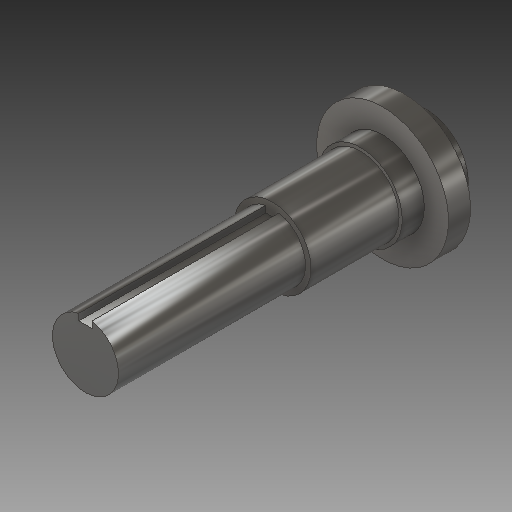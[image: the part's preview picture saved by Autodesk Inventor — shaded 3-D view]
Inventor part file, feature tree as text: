
AUTODESK INVENTOR PART (.ipt)
format: ipt  version: 2019 (Build 230136000, 136)  size: 175,616 bytes
history: native  units: mm
features: extrude x5, sketch x5, plane x1
ambient origin geometry x8: Origin, YZ Plane, XZ Plane, XY Plane, X Axis, Y Axis, Z Axis, Center Point
bodies: Solid1 (feature_tree)
feature tree (11):
  extrude  "Extrusion1"  Depth=30.0mm TaperAngle=0.0deg
  plane  "Work Plane1"
  extrude  "Extrusion2"  Depth=60.0mm
  extrude  "Extrusion3"  Depth=10.0mm
  extrude  "Extrusion4"  Depth=30.0mm
  extrude  "Extrusion5"  Depth=85.0mm
  sketch  "Sketch1"  dims[d0=38.0mm d1=30.0mm d2=0.0mm]
  sketch  "Sketch2"  dims[d3=-10.0mm d4=60.0mm]
  sketch  "Sketch3"  dims[d5=10.0mm d6=0.0mm d7=35.0mm]
  sketch  "Sketch4"  dims[d8=40.0mm d9=0.0mm d10=30.0mm]
  sketch  "Sketch5"  dims[d11=85.0mm d12=0.0mm d15=3.0mm d16=6.0mm d17=85.0mm d18=0.0mm]
